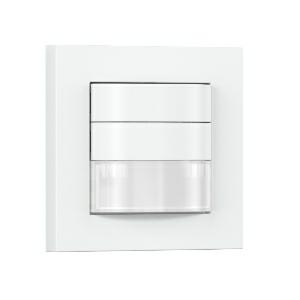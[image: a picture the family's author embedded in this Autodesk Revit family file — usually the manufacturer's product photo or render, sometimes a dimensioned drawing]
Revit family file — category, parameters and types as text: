
# Revit family: hf_180_032883
name_source: partatom
category: Elektroinstallationen
revit_build: Autodesk Revit 2016 (Build: 20190508_0715(x64)
units: mm (PartAtom-declared; Revit-internal decimal feet)

## family parameters
Basisbauteil = Fläche
Beim Laden mit Abzugskörper schneiden = Nein
Bemaßung runder Anschluss = Durchmesser verwenden
Beschriftungsausrichtung beibehalten = Nein
Gemeinsam genutzt = Nein
Raumberechnungspunkt = Nein
Teiletyp = Normal

## types (1)
- HF 180
    Apparent Load = 0 VA
    Beschreibung = Type: Presence detector; Dimensions (L x W x H): 21 x 80 x 80 mm; Mains power supply: 220 – 240 V / 50 – 60 Hz; Sensor Technology: High frequency; Application, place: Indoors; Application, room: one-person office, corridor / aisle, function room / ancillary room, kitchenette, stairwell, WC / washroom, Indoors; Installation site: wall; Installation: Concealed wiring; HF-system: 5,8 GHz; Electronic scalability: Yes; Mechanical scalability: No; Mounting height: 1,20 – 2,20 m; Optimum mounting height: 1,2 m; Detection: also through glass, wood and stud walls; Detection angle: 180 °; Angle of aperture: 140 °; Sneak-by guard: Yes; Reach, radial: r = 8 m (101 m²); Reach, tangential: r = 8 m (101 m²); Twilight setting TEACH: Yes; Twilight setting: 2 – 1000 lx; Time setting: 30 sec – 30 min; Switching output 1, resistive: 2000 W; Switching output 1, number of LEDs / fluorescent lamps: 8 pcs.; Constant-lighting control: No; Basic light level function: No; Functions: Normal / test mode, Semi-/fully automatic, Switch active / switch inactive, Manual ON / ON-OFF; Settings via: Remote control, DIP switches, Potentiometers, Smart Remote; With remote control: No; Interconnection: Yes; IP-rating: IP20; Material: Plastic; Ambient temperature: 0 – 40 °C; Colour: white; Colour, RAL: 9010; Manufacturer's Warranty: 5 years; Version: COM1 - white; PU1, EAN: 4007841032883
    Height = 80 mm  [stored 0.262467 ft]
    Hersteller = Steinel
    Length = 21 mm
    Maximum range = 7.902 m
    ModVariant = Nein
    Modell = 032883
    Mounting Type = Recessed
    Number of Poles = 1
    OnlyDefault = Ja
    Power Factor = 1
    Product Name = HF 180
    Product group = Sensor-switched indoor light
    ProductGroupID = 30
    Protection Class = Protection class
    Protection Degree = IP 20
    RlxData = <blob elided: 124569 chars, md5=6e02e099>
    Sensor characteristics = Sector <145°
    Sensor type = HF
    SensorDataFile = <blob elided: 8545 chars, md5=53bc5c10>
    Type of entry = Motion
    Typenbild = produkt1_032883.jpg
    Typenkommentare = Product without accessories
    URL = http://relux.com
    VarID = ---
    Voltage = 0 V
    Vorgabe-Ansicht = 1800 mm
    Weight = 0.00 kg
    Width = 80 mm  [stored 0.262467 ft]

note: [stored X ft] marks values corroborated as IEEE doubles in the binary element streams (Revit-internal decimal feet)

## geometry (parser evidence)
native form markers: Blend x4, Sweep x16
no freeform markers — native parametric forms only
